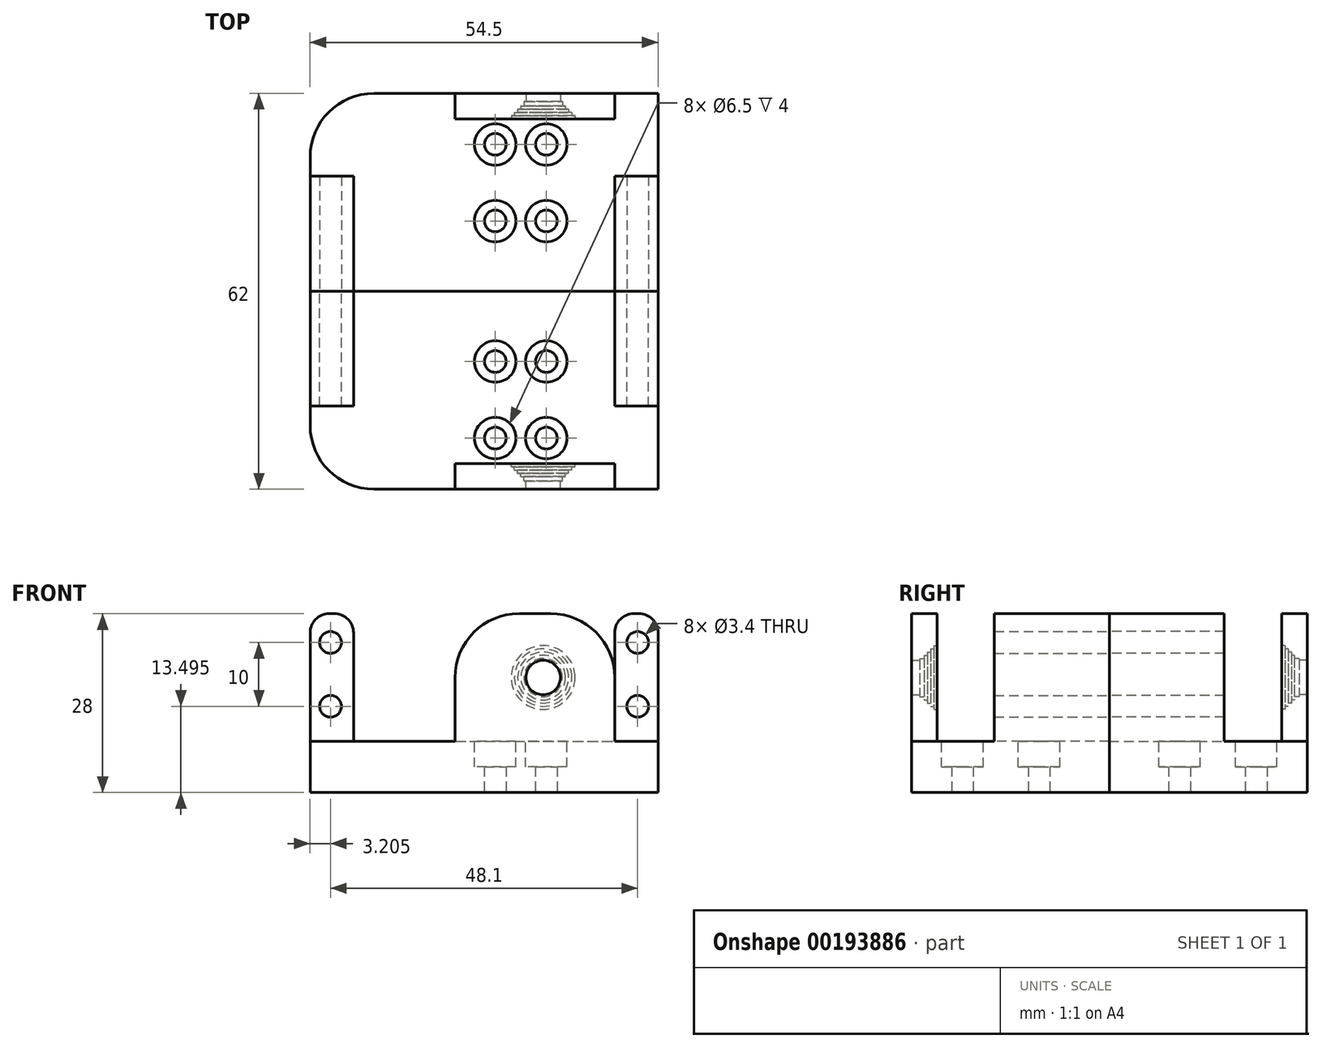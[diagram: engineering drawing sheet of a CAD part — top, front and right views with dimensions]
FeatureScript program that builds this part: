
annotation { "Feature Type Name" : "Feature", "Feature Type Description" : "" }
export const myFeature = defineFeature(function(context is Context, id is Id, definition is map)
    precondition{}
    {
        {
            var Q0;
            Q0=qCreatedBy(makeId("Front.planeOp"),FACE);
            var sketch = newSketch(context, id + "F0", { "sketchPlane" : qUnion([Q0])});
            skLineSegment(sketch, "E0.bottom", {"start": v(-17.34, 11.43) * mm, "end": v(37.16, 11.43) * mm});
            skLineSegment(sketch, "E0.top", {"start": v(-17.34, 19.43) * mm, "end": v(37.16, 19.43) * mm});
            skLineSegment(sketch, "E0.left", {"start": v(-17.34, 11.43) * mm, "end": v(-17.34, 19.43) * mm});
            skLineSegment(sketch, "E0.right", {"start": v(37.16, 11.43) * mm, "end": v(37.16, 19.43) * mm});
            skSolve(sketch);
        }
        {
            var Q0;
            Q0 = qSketchRegion(id + "F0", true);
            extrude(context, id + "F1", {"entities" : qUnion([Q0]), "depth" : 31 * mm});
        }
        {
            var Q0;
            Q0=makeQuery(id+"F1.opExtrude","SWEPT_FACE",FACE,{"disambiguationData":[OSD([sQuery(id+"F0.wireOp",EDGE,"E0.top")])]});
            var sketch = newSketch(context, id + "F2", { "sketchPlane" : qUnion([Q0])});
            skLineSegment(sketch, "E1.0", {"start": v(-17.34, 0) * mm, "end": v(37.16, 0) * mm});
            skLineSegment(sketch, "E2.0", {"start": v(-17.34, -31) * mm, "end": v(37.16, -31) * mm});
            skLineSegment(sketch, "E3.bottom", {"start": v(-17.34, 0) * mm, "end": v(-10.54, 0) * mm});
            skLineSegment(sketch, "E3.top", {"start": v(-17.34, -18) * mm, "end": v(-10.54, -18) * mm});
            skLineSegment(sketch, "E3.left", {"start": v(-17.34, 0) * mm, "end": v(-17.34, -18) * mm});
            skLineSegment(sketch, "E3.right", {"start": v(-10.54, 0) * mm, "end": v(-10.54, -18) * mm});
            skLineSegment(sketch, "E4.bottom", {"start": v(37.16, 0) * mm, "end": v(30.36, 0) * mm});
            skLineSegment(sketch, "E4.top", {"start": v(37.16, -18) * mm, "end": v(30.36, -18) * mm});
            skLineSegment(sketch, "E4.left", {"start": v(37.16, 0) * mm, "end": v(37.16, -18) * mm});
            skLineSegment(sketch, "E4.right", {"start": v(30.36, 0) * mm, "end": v(30.36, -18) * mm});
            skLineSegment(sketch, "E5.bottom", {"start": v(5.36, -31) * mm, "end": v(30.36, -31) * mm});
            skLineSegment(sketch, "E5.top", {"start": v(5.36, -27) * mm, "end": v(30.36, -27) * mm});
            skLineSegment(sketch, "E5.left", {"start": v(5.36, -31) * mm, "end": v(5.36, -27) * mm});
            skLineSegment(sketch, "E5.right", {"start": v(30.36, -31) * mm, "end": v(30.36, -27) * mm});
            skSolve(sketch);
        }
        {
            var Q0;
            Q0 = qSketchRegion(id + "F2", true);
            extrude(context, id + "F3", {"entities" : qUnion([Q0]), "operationType" : NewBodyOperationType.ADD, "depth" : 20 * mm});
        }
        {
            var Q0;
            Q0=makeQuery(id+"F1.opExtrude","SWEPT_FACE",FACE,{"disambiguationData":[OSD([sQuery(id+"F0.wireOp",EDGE,"E0.bottom")])]});
            var sketch = newSketch(context, id + "F4", { "sketchPlane" : qUnion([Q0])});
            skCircle(sketch, "E6", {"center": v(19.66, 11) * mm, "radius": 1.7 * mm});
            skCircle(sketch, "E7", {"center": v(11.66, 11) * mm, "radius": 1.7 * mm});
            skCircle(sketch, "E8", {"center": v(19.66, 23) * mm, "radius": 1.7 * mm});
            skCircle(sketch, "E9", {"center": v(11.66, 23) * mm, "radius": 1.7 * mm});
            skLineSegment(sketch, "E10.0", {"start": v(-17.34, 31) * mm, "end": v(-17.34, 0) * mm});
            skSolve(sketch);
        }
        {
            var Q0;
            Q0 = qSketchRegion(id + "F4", true);
            extrude(context, id + "F5", {"entities" : qUnion([Q0]), "operationType" : NewBodyOperationType.REMOVE, "endBound" : BoundingType.THROUGH_ALL, "oppositeDirection" : true, "depth" : 25 * mm});
        }
        {
            var Q0;
            Q0=makeQuery(id+"F1.opExtrude","SWEPT_FACE",FACE,{"disambiguationData":[OSD([sQuery(id+"F0.wireOp",EDGE,"E0.top")])]});
            var sketch = newSketch(context, id + "F6", { "sketchPlane" : qUnion([Q0])});
            skCircle(sketch, "E11.0", {"center": v(11.66, -11) * mm, "radius": 1.7 * mm});
            skCircle(sketch, "E12.0", {"center": v(19.66, -11) * mm, "radius": 1.7 * mm});
            skCircle(sketch, "E13.0", {"center": v(19.66, -23) * mm, "radius": 1.7 * mm});
            skCircle(sketch, "E14.0", {"center": v(11.66, -23) * mm, "radius": 1.7 * mm});
            skCircle(sketch, "E15", {"center": v(11.66, -11) * mm, "radius": 3.25 * mm});
            skCircle(sketch, "E16", {"center": v(19.66, -11) * mm, "radius": 3.25 * mm});
            skCircle(sketch, "E17", {"center": v(19.66, -23) * mm, "radius": 3.25 * mm});
            skCircle(sketch, "E18", {"center": v(11.66, -23) * mm, "radius": 3.25 * mm});
            skSolve(sketch);
        }
        {
            var Q0;
            Q0 = qSketchRegion(id + "F6", true);
            extrude(context, id + "F7", {"entities" : qUnion([Q0]), "operationType" : NewBodyOperationType.REMOVE, "oppositeDirection" : true, "depth" : 4 * mm});
        }
        {
            var Q0;
            Q0=makeQuery(id+"F3.boolean.opBoolean","MERGE",FACE,{"derivedFrom":[makeQuery(id+"F1.opExtrude","CAP_FACE",FACE,{"disambiguationData":[OSD([sQuery(id+"F0.wireOp",EDGE,"E0.bottom"),sQuery(id+"F0.wireOp",EDGE,"E0.top"),sQuery(id+"F0.wireOp",EDGE,"E0.left"),sQuery(id+"F0.wireOp",EDGE,"E0.right")])],"isStart":true}),makeQuery(id+"F3.opExtrude","SWEPT_FACE",FACE,{"disambiguationData":[OSD([sQuery(id+"F2.wireOp",EDGE,"E3.bottom")])]}),makeQuery(id+"F3.opExtrude","SWEPT_FACE",FACE,{"disambiguationData":[OSD([sQuery(id+"F2.wireOp",EDGE,"E4.bottom")])]})]});
            var sketch = newSketch(context, id + "F8", { "sketchPlane" : qUnion([Q0])});
            skCircle(sketch, "E19", {"center": v(14.14, 24.93) * mm, "radius": 1.7 * mm});
            skCircle(sketch, "E20", {"center": v(14.14, 34.93) * mm, "radius": 1.7 * mm});
            skCircle(sketch, "E21", {"center": v(-33.96, 24.93) * mm, "radius": 1.7 * mm});
            skCircle(sketch, "E22", {"center": v(-33.96, 34.93) * mm, "radius": 1.7 * mm});
            skLineSegment(sketch, "E23.0", {"start": v(17.34, 11.43) * mm, "end": v(17.34, 39.43) * mm});
            skLineSegment(sketch, "E24.0", {"start": v(-37.16, 11.43) * mm, "end": v(-37.16, 39.43) * mm});
            skSolve(sketch);
        }
        {
            var Q0;
            Q0 = qSketchRegion(id + "F8", true);
            extrude(context, id + "F9", {"entities" : qUnion([Q0]), "operationType" : NewBodyOperationType.REMOVE, "endBound" : BoundingType.THROUGH_ALL, "oppositeDirection" : true, "depth" : 25 * mm});
        }
        {
            var Q0;
            Q0=makeQuery(id+"F3.opExtrude","SWEPT_FACE",FACE,{"disambiguationData":[OSD([sQuery(id+"F2.wireOp",EDGE,"E5.top")])]});
            var sketch = newSketch(context, id + "F10", { "sketchPlane" : qUnion([Q0])});
            skCircle(sketch, "E25", {"center": v(-19.16, 29.43) * mm, "radius": 2.7 * mm});
            skLineSegment(sketch, "E26.0", {"start": v(-30.36, 39.43) * mm, "end": v(-30.36, 19.43) * mm});
            skSolve(sketch);
        }
        {
            var Q0;
            Q0 = qSketchRegion(id + "F10", true);
            extrude(context, id + "F11", {"entities" : qUnion([Q0]), "operationType" : NewBodyOperationType.REMOVE, "endBound" : BoundingType.THROUGH_ALL, "oppositeDirection" : true, "depth" : 25 * mm});
        }
        {
            var Q0;
            Q0=makeQuery(id+"F3.opExtrude","SWEPT_FACE",FACE,{"disambiguationData":[OSD([sQuery(id+"F2.wireOp",EDGE,"E5.top")])]});
            var sketch = newSketch(context, id + "F12", { "sketchPlane" : qUnion([Q0])});
            skCircle(sketch, "E27.0", {"center": v(-19.16, 29.43) * mm, "radius": 2.7 * mm});
            skCircle(sketch, "E28", {"center": v(-19.16, 29.43) * mm, "radius": 5 * mm});
            skSolve(sketch);
        }
        {
            var Q0;
            Q0 = qSketchRegion(id + "F12", true);
            extrude(context, id + "F13", {"entities" : qUnion([Q0]), "operationType" : NewBodyOperationType.REMOVE, "oppositeDirection" : true, "depth" : 0.5 * mm});
        }
        {
            var Q0;
            Q0=makeQuery(id+"F13.boolean.opBoolean","COPY",FACE,{"derivedFrom":makeQuery(id+"F13.opExtrude","CAP_FACE",FACE,{"disambiguationData":[OSD([sQuery(id+"F12.wireOp",EDGE,"E27.0"),sQuery(id+"F12.wireOp",EDGE,"E28")])],"isStart":false})});
            var sketch = newSketch(context, id + "F14", { "sketchPlane" : qUnion([Q0])});
            skCircle(sketch, "E29.0", {"center": v(-19.16, 29.43) * mm, "radius": 2.7 * mm});
            skCircle(sketch, "E30", {"center": v(-19.16, 29.43) * mm, "radius": 4.5 * mm});
            skSolve(sketch);
        }
        {
            var Q0;
            Q0 = qSketchRegion(id + "F14", true);
            extrude(context, id + "F15", {"entities" : qUnion([Q0]), "operationType" : NewBodyOperationType.REMOVE, "oppositeDirection" : true, "depth" : 0.5 * mm});
        }
        {
            var Q0;
            Q0=makeQuery(id+"F15.boolean.opBoolean","COPY",FACE,{"derivedFrom":makeQuery(id+"F15.opExtrude","CAP_FACE",FACE,{"disambiguationData":[OSD([sQuery(id+"F14.wireOp",EDGE,"E29.0"),sQuery(id+"F14.wireOp",EDGE,"E30")])],"isStart":false})});
            var sketch = newSketch(context, id + "F16", { "sketchPlane" : qUnion([Q0])});
            skCircle(sketch, "E31.0", {"center": v(-19.16, 29.43) * mm, "radius": 2.7 * mm});
            skCircle(sketch, "E32", {"center": v(-19.16, 29.43) * mm, "radius": 4 * mm});
            skSolve(sketch);
        }
        {
            var Q0;
            Q0 = qSketchRegion(id + "F16", true);
            extrude(context, id + "F17", {"entities" : qUnion([Q0]), "operationType" : NewBodyOperationType.REMOVE, "oppositeDirection" : true, "depth" : 0.5 * mm});
        }
        {
            var Q0;
            Q0=makeQuery(id+"F17.boolean.opBoolean","COPY",FACE,{"derivedFrom":makeQuery(id+"F17.opExtrude","CAP_FACE",FACE,{"disambiguationData":[OSD([sQuery(id+"F16.wireOp",EDGE,"E31.0"),sQuery(id+"F16.wireOp",EDGE,"E32")])],"isStart":false})});
            var sketch = newSketch(context, id + "F18", { "sketchPlane" : qUnion([Q0])});
            skCircle(sketch, "E33.0", {"center": v(-19.16, 29.43) * mm, "radius": 2.7 * mm});
            skCircle(sketch, "E34", {"center": v(-19.16, 29.43) * mm, "radius": 3.5 * mm});
            skSolve(sketch);
        }
        {
            var Q0;
            Q0 = qSketchRegion(id + "F18", true);
            extrude(context, id + "F19", {"entities" : qUnion([Q0]), "operationType" : NewBodyOperationType.REMOVE, "oppositeDirection" : true, "depth" : 0.5 * mm});
        }
        {
            var Q0;
            Q0=makeQuery(id+"F19.boolean.opBoolean","COPY",FACE,{"derivedFrom":makeQuery(id+"F19.opExtrude","CAP_FACE",FACE,{"disambiguationData":[OSD([sQuery(id+"F18.wireOp",EDGE,"E33.0"),sQuery(id+"F18.wireOp",EDGE,"E34")])],"isStart":false})});
            var sketch = newSketch(context, id + "F20", { "sketchPlane" : qUnion([Q0])});
            skCircle(sketch, "E35.0", {"center": v(-19.16, 29.43) * mm, "radius": 2.7 * mm});
            skCircle(sketch, "E36", {"center": v(-19.16, 29.43) * mm, "radius": 3 * mm});
            skSolve(sketch);
        }
        {
            var Q0;
            Q0 = qSketchRegion(id + "F20", true);
            extrude(context, id + "F21", {"entities" : qUnion([Q0]), "operationType" : NewBodyOperationType.REMOVE, "oppositeDirection" : true, "depth" : 0.7 * mm});
        }
        {
            var Q0;
            Q0=makeQuery(id+"F3.opExtrude","CAP_EDGE",EDGE,{"disambiguationData":[OSD([sQuery(id+"F2.wireOp",EDGE,"E3.left")])],"isStart":false});
            var Q1;
            Q1=makeQuery(id+"F3.opExtrude","CAP_EDGE",EDGE,{"disambiguationData":[OSD([sQuery(id+"F2.wireOp",EDGE,"E3.right")])],"isStart":false});
            var Q2;
            Q2=makeQuery(id+"F3.opExtrude","CAP_EDGE",EDGE,{"disambiguationData":[OSD([sQuery(id+"F2.wireOp",EDGE,"E4.right")])],"isStart":false});
            var Q3;
            Q3=makeQuery(id+"F3.opExtrude","CAP_EDGE",EDGE,{"disambiguationData":[OSD([sQuery(id+"F2.wireOp",EDGE,"E4.left")])],"isStart":false});
            fillet(context, id + "F22", {"entities" : qUnion([Q0, Q1, Q2, Q3]), "radius" : 3 * mm, "tangentPropagation" : true, "allowEdgeOverflow" : false});
        }
        {
            var Q0;
            Q0=makeQuery(id+"F3.opExtrude","CAP_EDGE",EDGE,{"disambiguationData":[OSD([sQuery(id+"F2.wireOp",EDGE,"E5.left")])],"isStart":false});
            var Q1;
            Q1=makeQuery(id+"F3.opExtrude","CAP_EDGE",EDGE,{"disambiguationData":[OSD([sQuery(id+"F2.wireOp",EDGE,"E5.right")])],"isStart":false});
            fillet(context, id + "F23", {"entities" : qUnion([Q0, Q1]), "radius" : 10 * mm, "tangentPropagation" : true, "allowEdgeOverflow" : false});
        }
        {
            var Q0;
            Q0=makeQuery(id+"F1.opExtrude","CAP_EDGE",EDGE,{"disambiguationData":[OSD([sQuery(id+"F0.wireOp",EDGE,"E0.left")])],"isStart":false});
            fillet(context, id + "F24", {"entities" : qUnion([Q0]), "radius" : 10 * mm, "tangentPropagation" : true, "allowEdgeOverflow" : false});
        }
        {
            var Q0;
            Q0=makeQuery(id+"F1.opExtrude","SWEPT_BODY",BODY,{"disambiguationData":[OSD([sQuery(id+"F0.wireOp",EDGE,"E0.bottom"),sQuery(id+"F0.wireOp",EDGE,"E0.top"),sQuery(id+"F0.wireOp",EDGE,"E0.left"),sQuery(id+"F0.wireOp",EDGE,"E0.right")])]});
            var Q1;
            Q1=qCreatedBy(makeId("Front.planeOp"),FACE);
            mirror(context, id + "F25", {"entities" : qUnion([Q0]), "mirrorPlane" : qUnion([Q1])});
        }
    });
